# Revit family: 32L 2 to 6 units single sided indoor manifold system REVISED
name_source: partatom
category: Plumbing Fixtures
revit_build: Autodesk Revit 2016 (Build: 20150220_1215(x64)
units: mm (PartAtom-declared; Revit-internal decimal feet)

## family parameters
Always vertical = Yes
Cut with Voids When Loaded = No
Part Type = Normal
Room Calculation Point = No
Round Connector Dimension = Use Diameter
Shared = No
Work Plane-Based = No

## types (10) — shared parameters
Cold Water Inlet Pipe connector description = Male threaded connector R1-1/2"
Cold Water Inlet Pipe diameter = 38.1mm(DN 40)
Exhaust Air pipe connector description = Exhaust air  connector
Exhaust Air pipe diameter = 100 mm
Gas Inlet Pipe connector description = Male threaded connector R1-1/2"
Gas Inlet Pipe diameter = 38.1mm(DN 40)
Hot Water Outlet Pipe connector description = Male threaded connector R1-1/2"
Hot Water Outlet Pipe diameter = 38.1mm(DN 40)
Supply Air/Air Inlet pipe connector description = Air Inlet  connector
Supply Air/Air Inlet pipe diameter = 100 mm

## per-type parameters (varying)
- 32L 2 units single sided indoor floor mounted: 2 Unit L=Yes; 2 Unit R=No; 3 Unit L=No; 3 Unit R=No; Array Offset=490 mm; Base Offset L=1040 mm; Base Offset R=1040 mm; Base Support L=Yes; Base Support R=No; Connector Left=1030 mm; Connector Right=0 mm; D1=1815 mm; D2=275 mm; D3=1815 mm; No of Connectors 1=2; No of Connectors 2=2; No. of power supply point required=2; Nominal depth=900mm; Nominal height=1540mm; Nominal width=1040mm; Number of Gas Water Heaters=2; Product SKU Dux brand=D23200FN/LFx; Product SKU Thermann brand=T23200FN/LFx; Product description=Gas Water heater Manifold 2 unit indoor floor mounted; Total Max. power requirement=446W; Total nominal gas consumption (MJ/h)=434; Total number of Exhaust Air connector=2; Total number of Supply Air/Air Inlet connector=2; Unit Offset=41 mm; Weight (Kg)=110
- 32L 3 units single sided indoor floor mounted: 2 Unit L=No; 2 Unit R=No; 3 Unit L=Yes; 3 Unit R=No; Array Offset=980 mm; Base Offset L=1540 mm; Base Offset R=1040 mm; Base Support L=Yes; Base Support R=No; Connector Left=1530 mm; Connector Right=0 mm; D1=1820 mm; D2=280 mm; D3=1820 mm; No of Connectors 1=3; No of Connectors 2=3; No. of power supply point required=3; Nominal depth=900mm; Nominal height=1540mm; Nominal width=1540mm; Number of Gas Water Heaters=3; Product SKU Dux brand=D33200FN/LFx; Product SKU Thermann brand=T33200FN/LFx; Product description=Gas Water heater Manifold 3 unit indoor floor mounted; Total Max. power requirement=669W; Total nominal gas consumption (MJ/h)=651; Total number of Exhaust Air connector=3; Total number of Supply Air/Air Inlet connector=3; Unit Offset=41 mm; Weight (Kg)=140
- 32L 4 units single sided indoor floor mounted: 2 Unit L=Yes; 2 Unit R=Yes; 3 Unit L=No; 3 Unit R=No; Array Offset=490 mm; Base Offset L=1040 mm; Base Offset R=1040 mm; Base Support L=Yes; Base Support R=Yes; Connector Left=1030 mm; Connector Right=1040 mm; D1=775 mm; D2=275 mm; D3=775 mm; No of Connectors 1=2; No of Connectors 2=2; No. of power supply point required=4; Nominal depth=900mm; Nominal height=1540mm; Nominal width=2080mm; Number of Gas Water Heaters=4; Product SKU Dux brand=D43200FN/LFx; Product SKU Thermann brand=T43200FN/LFx; Product description=Gas Water heater Manifold 4 unit indoor floor mounted; Total Max. power requirement=892W; Total nominal gas consumption (MJ/h)=868; Total number of Exhaust Air connector=4; Total number of Supply Air/Air Inlet connector=4; Unit Offset=41 mm; Weight (Kg)=220
- 32L 5 units single sided indoor floor mounted: 2 Unit L=No; 2 Unit R=Yes; 3 Unit L=Yes; 3 Unit R=No; Array Offset=980 mm; Base Offset L=1540 mm; Base Offset R=1040 mm; Base Support L=Yes; Base Support R=Yes; Connector Left=1530 mm; Connector Right=1040 mm; D1=775 mm; D2=280 mm; D3=1820 mm; No of Connectors 1=2; No of Connectors 2=3; No. of power supply point required=5; Nominal depth=900mm; Nominal height=1540mm; Nominal width=2580mm; Number of Gas Water Heaters=5; Product SKU Dux brand=D53200FN/LFx; Product SKU Thermann brand=T53200FN/LFx; Product description=Gas Water heater Manifold 5 unit indoor floor mounted; Total Max. power requirement=1115W; Total nominal gas consumption (MJ/h)=1085; Total number of Exhaust Air connector=5; Total number of Supply Air/Air Inlet connector=5; Unit Offset=41 mm; Weight (Kg)=250
- 32L 6 units single sided indoor floor mounted: 2 Unit L=No; 2 Unit R=No; 3 Unit L=Yes; 3 Unit R=Yes; Array Offset=1540 mm; Base Offset L=1540 mm; Base Offset R=1540 mm; Base Support L=Yes; Base Support R=Yes; Connector Left=1530 mm; Connector Right=1540 mm; D1=280 mm; D2=280 mm; D3=1260 mm; No of Connectors 1=3; No of Connectors 2=3; No. of power supply point required=6; Nominal depth=900mm; Nominal height=1540mm; Nominal width=3080mm; Number of Gas Water Heaters=6; Product SKU Dux brand=D63200FN/LFx; Product SKU Thermann brand=T63200FN/LFx; Product description=Gas Water heater Manifold 6 unit  indoor floor mounted; Total Max. power requirement=1338W; Total nominal gas consumption (MJ/h)=1302; Total number of Exhaust Air connector=6; Total number of Supply Air/Air Inlet connector=6; Unit Offset=41 mm; Weight (Kg)=280
- 32L 2 units single sided indoor wall mounted: 2 Unit L=Yes; 2 Unit R=No; 3 Unit L=No; 3 Unit R=No; Array Offset=490 mm; Base Offset L=1040 mm; Base Offset R=1040 mm; Base Support L=No; Base Support R=No; Connector Left=1030 mm; Connector Right=0 mm; D1=1815 mm; D2=275 mm; D3=1815 mm; No of Connectors 1=2; No of Connectors 2=2; No. of power supply point required=2; Nominal depth=295mm; Nominal height=1500mm; Nominal width=1040mm; Number of Gas Water Heaters=2; Product SKU Dux brand=D23200FN/LWx; Product SKU Thermann brand=T23200FN/LWx; Product description=Gas Water heater Manifold 2 unit indoor wall mounted; Total Max. power requirement=446W; Total nominal gas consumption (MJ/h)=434; Total number of Exhaust Air connector=2; Total number of Supply Air/Air Inlet connector=2; Unit Offset=0 mm; Weight (Kg)=110
- 32L 3 units single sided indoor wall mounted: 2 Unit L=No; 2 Unit R=No; 3 Unit L=Yes; 3 Unit R=No; Array Offset=980 mm; Base Offset L=1540 mm; Base Offset R=1040 mm; Base Support L=No; Base Support R=No; Connector Left=1530 mm; Connector Right=0 mm; D1=1820 mm; D2=280 mm; D3=1820 mm; No of Connectors 1=3; No of Connectors 2=3; No. of power supply point required=3; Nominal depth=295mm; Nominal height=1500mm; Nominal width=1540mm; Number of Gas Water Heaters=3; Product SKU Dux brand=D33200FN/LWx; Product SKU Thermann brand=T33200FN/LWx; Product description=Gas Water heater Manifold 3 unit indoor wall mounted; Total Max. power requirement=669W; Total nominal gas consumption (MJ/h)=651; Total number of Exhaust Air connector=3; Total number of Supply Air/Air Inlet connector=3; Unit Offset=0 mm; Weight (Kg)=140
- 32L 4 units single sided indoor wall mounted: 2 Unit L=Yes; 2 Unit R=Yes; 3 Unit L=No; 3 Unit R=No; Array Offset=490 mm; Base Offset L=1040 mm; Base Offset R=1040 mm; Base Support L=No; Base Support R=No; Connector Left=1030 mm; Connector Right=1040 mm; D1=775 mm; D2=275 mm; D3=775 mm; No of Connectors 1=2; No of Connectors 2=2; No. of power supply point required=4; Nominal depth=295mm; Nominal height=1500mm; Nominal width=2080mm; Number of Gas Water Heaters=4; Product SKU Dux brand=D43200FN/LWx; Product SKU Thermann brand=T43200FN/LWx; Product description=Gas Water heater Manifold 4 unit indoor wall mounted; Total Max. power requirement=892W; Total nominal gas consumption (MJ/h)=868; Total number of Exhaust Air connector=4; Total number of Supply Air/Air Inlet connector=4; Unit Offset=0 mm; Weight (Kg)=220
- 32L 5 units single sided indoor wall mounted: 2 Unit L=No; 2 Unit R=Yes; 3 Unit L=Yes; 3 Unit R=No; Array Offset=980 mm; Base Offset L=1540 mm; Base Offset R=1040 mm; Base Support L=No; Base Support R=No; Connector Left=1530 mm; Connector Right=1040 mm; D1=775 mm; D2=280 mm; D3=1820 mm; No of Connectors 1=2; No of Connectors 2=3; No. of power supply point required=5; Nominal depth=295mm; Nominal height=1500mm; Nominal width=2580mm; Number of Gas Water Heaters=5; Product SKU Dux brand=D53200FN/LWx; Product SKU Thermann brand=T53200FN/LWx; Product description=Gas Water heater Manifold 5 unit  indoor wall mounted; Total Max. power requirement=1115W; Total nominal gas consumption (MJ/h)=1085; Total number of Exhaust Air connector=5; Total number of Supply Air/Air Inlet connector=5; Unit Offset=0 mm; Weight (Kg)=250
- 32L 6 units single sided indoor wall mounted: 2 Unit L=No; 2 Unit R=No; 3 Unit L=Yes; 3 Unit R=Yes; Array Offset=1540 mm; Base Offset L=1040 mm; Base Offset R=1040 mm; Base Support L=No; Base Support R=No; Connector Left=1530 mm; Connector Right=1540 mm; D1=280 mm; D2=280 mm; D3=1260 mm; No of Connectors 1=3; No of Connectors 2=3; No. of power supply point required=6; Nominal depth=295mm; Nominal height=1500mm; Nominal width=3080mm; Number of Gas Water Heaters=6; Product SKU Dux brand=D63200FN/LWx; Product SKU Thermann brand=T63200FN/LWx; Product description=Gas Water heater Manifold 6 unit indoor wall mounted; Total Max. power requirement=1338W; Total nominal gas consumption (MJ/h)=1302; Total number of Exhaust Air connector=6; Total number of Supply Air/Air Inlet connector=6; Unit Offset=0 mm; Weight (Kg)=280

## geometry (parser evidence)
native form markers: Sweep x17
no freeform markers — native parametric forms only
